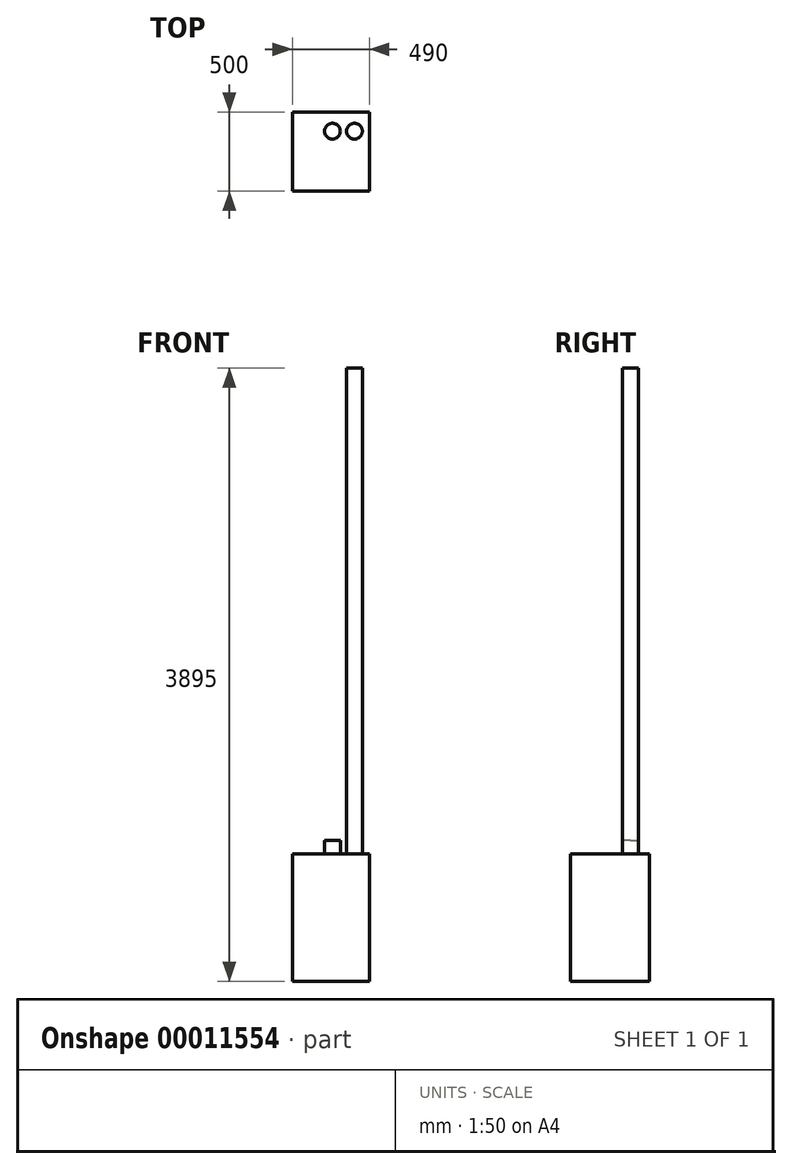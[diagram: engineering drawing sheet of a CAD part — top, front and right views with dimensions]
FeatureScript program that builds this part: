
annotation { "Feature Type Name" : "Feature", "Feature Type Description" : "" }
export const myFeature = defineFeature(function(context is Context, id is Id, definition is map)
    precondition{}
    {
        {
            var Q0;
            Q0=qCreatedBy(makeId("Front.planeOp"),FACE);
            var sketch = newSketch(context, id + "F0", { "sketchPlane" : qUnion([Q0])});
            skLineSegment(sketch, "E0.rect.bottom", {"start": v(245, 405) * mm, "end": v(-245, 405) * mm});
            skLineSegment(sketch, "E0.rect.top", {"start": v(245, -405) * mm, "end": v(-245, -405) * mm});
            skLineSegment(sketch, "E0.rect.left", {"start": v(245, 405) * mm, "end": v(245, -405) * mm});
            skLineSegment(sketch, "E0.rect.right", {"start": v(-245, 405) * mm, "end": v(-245, -405) * mm});
            skPoint(sketch, "E0.rect.middle", {"position": v(0, 0) * mm});
            skSolve(sketch);
        }
        {
            var Q0;
            Q0=makeQuery(id+"F0.imprint","IMPRINT",FACE,{"disambiguationData":[TD([[makeQuery(id+"F0.imprint","IMPRINT",EDGE,{"derivedFrom":sQuery(id+"F0.wireOp",EDGE,"E0.rect.bottom")}),1.0]])]});
            extrude(context, id + "F1", {"entities" : qUnion([Q0]), "depth" : 500 * mm});
        }
        {
            var Q0;
            Q0=makeQuery(id+"F1.opExtrude","SWEPT_FACE",FACE,{"disambiguationData":[OSD([sQuery(id+"F0.wireOp",EDGE,"E0.rect.bottom")])]});
            var sketch = newSketch(context, id + "F2", { "sketchPlane" : qUnion([Q0])});
            skCircle(sketch, "E1", {"center": v(149.52, -120) * mm, "radius": 50 * mm});
            skCircle(sketch, "E2", {"center": v(9.52, -120) * mm, "radius": 50 * mm});
            skSolve(sketch);
        }
        {
            var Q0;
            Q0 = qSketchRegion(id + "F2", true);
            extrude(context, id + "F3", {"entities" : qUnion([Q0]), "operationType" : NewBodyOperationType.ADD, "depth" : 85 * mm});
        }
        {
            var Q0;
            Q0=makeQuery(id+"F3.opExtrude","CAP_FACE",FACE,{"disambiguationData":[OSD([sQuery(id+"F2.wireOp",EDGE,"E1")])],"isStart":false});
            extrude(context, id + "F4", {"entities" : qUnion([Q0]), "operationType" : NewBodyOperationType.ADD, "depth" : 3000 * mm});
        }
    });
